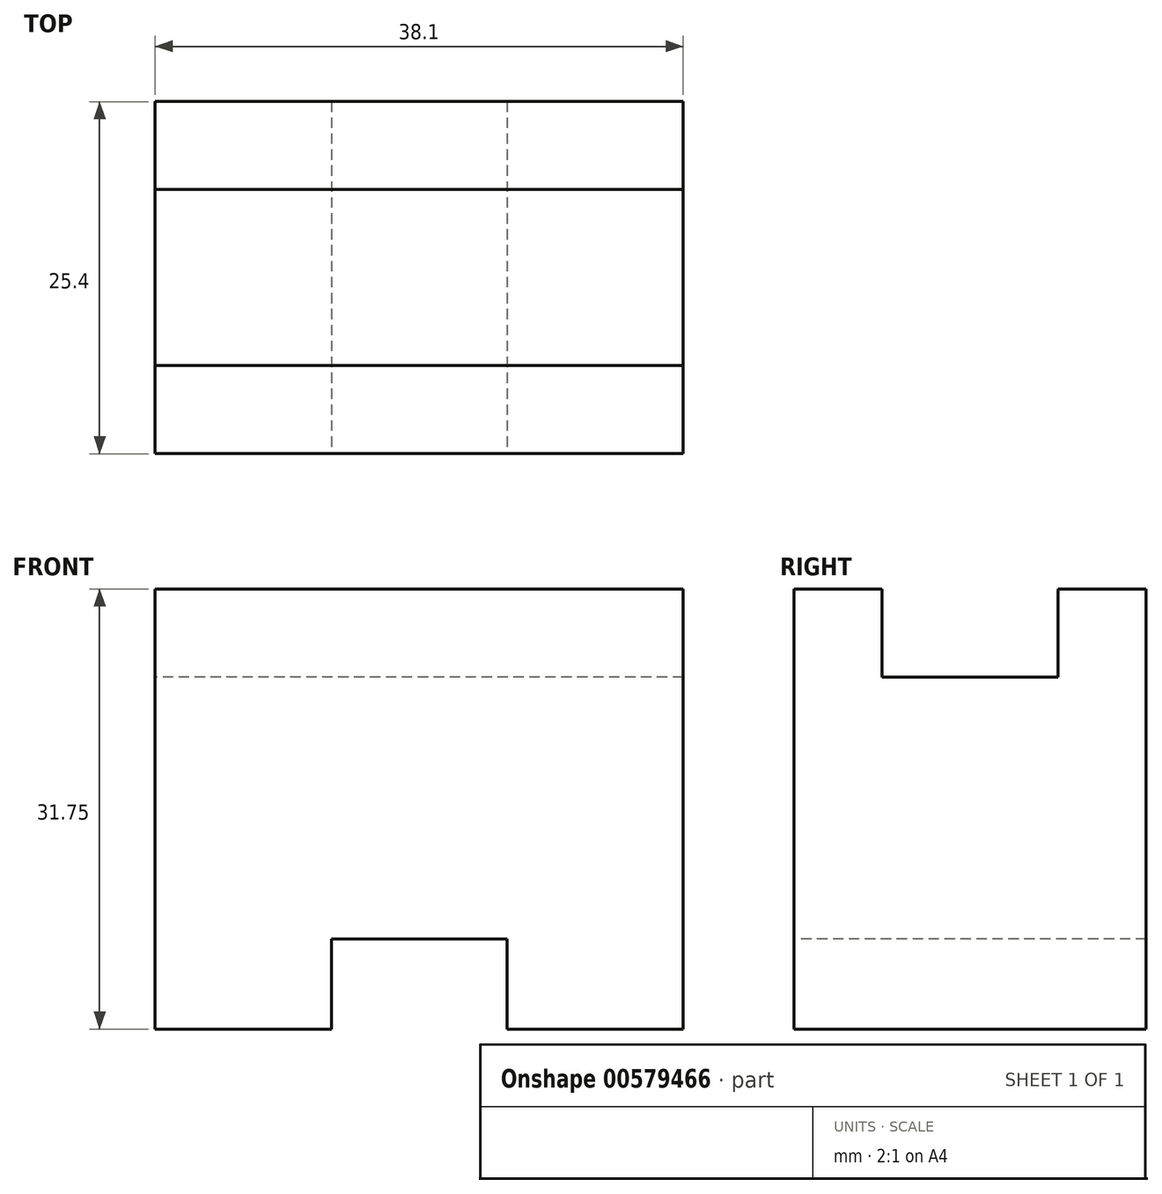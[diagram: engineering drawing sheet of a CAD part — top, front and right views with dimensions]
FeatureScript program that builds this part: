
annotation { "Feature Type Name" : "Feature", "Feature Type Description" : "" }
export const myFeature = defineFeature(function(context is Context, id is Id, definition is map)
    precondition{}
    {
        {
            var Q0;
            Q0=qCreatedBy(makeId("Right.planeOp"),FACE);
            var sketch = newSketch(context, id + "F0", { "sketchPlane" : qUnion([Q0])});
            skLineSegment(sketch, "E0", {"start": v(-37.44, 0) * mm, "end": v(-37.44, 31.75) * mm});
            skLineSegment(sketch, "E1", {"start": v(-37.44, 31.75) * mm, "end": v(-31.09, 31.75) * mm});
            skLineSegment(sketch, "E2", {"start": v(-31.09, 31.75) * mm, "end": v(-31.09, 25.4) * mm});
            skLineSegment(sketch, "E3", {"start": v(-31.09, 25.4) * mm, "end": v(-18.39, 25.4) * mm});
            skLineSegment(sketch, "E4", {"start": v(-18.39, 25.4) * mm, "end": v(-18.39, 31.75) * mm});
            skLineSegment(sketch, "E5", {"start": v(-18.39, 31.75) * mm, "end": v(-12.04, 31.75) * mm});
            skLineSegment(sketch, "E6", {"start": v(-12.04, 31.75) * mm, "end": v(-12.04, 0) * mm});
            skLineSegment(sketch, "E7", {"start": v(-12.04, 0) * mm, "end": v(-37.44, 0) * mm});
            skSolve(sketch);
        }
        {
            var Q0;
            Q0=makeQuery(id+"F0.imprint","IMPRINT",FACE,{"disambiguationData":[TD([[makeQuery(id+"F0.imprint","IMPRINT",EDGE,{"derivedFrom":sQuery(id+"F0.wireOp",EDGE,"E0")}),-1.0]])]});
            extrude(context, id + "F1", {"entities" : qUnion([Q0]), "depth" : 38.1 * mm, "offsetDistance" : 25.4 * mm});
        }
        {
            var Q0;
            Q0=makeQuery(id+"F1.opExtrude","SWEPT_FACE",FACE,{"disambiguationData":[OSD([sQuery(id+"F0.wireOp",EDGE,"E0")])]});
            var sketch = newSketch(context, id + "F2", { "sketchPlane" : qUnion([Q0])});
            skLineSegment(sketch, "E8", {"start": v(12.74, 0) * mm, "end": v(12.74, 6.49) * mm});
            skLineSegment(sketch, "E9", {"start": v(12.74, 6.49) * mm, "end": v(25.39, 6.49) * mm});
            skLineSegment(sketch, "E10", {"start": v(25.39, 6.49) * mm, "end": v(25.39, 0) * mm});
            skSolve(sketch);
        }
        {
            var Q0;
            Q0 = qSketchRegion(id + "F2", true);
            var Q1;
            {var subQ0=sQuery(id+"F2.wireOp",EDGE,"E8");Q1=makeQuery(id+"F2.imprint","IMPRINT",FACE,{"disambiguationData":[TD([[makeQuery(id+"F2.imprint","IMPRINT",EDGE,{"derivedFrom":subQ0}),-1.0]])]});}
            extrude(context, id + "F3", {"entities" : qUnion([Q0, Q1]), "operationType" : NewBodyOperationType.REMOVE, "endBound" : BoundingType.THROUGH_ALL, "oppositeDirection" : true, "depth" : 25.4 * mm, "offsetDistance" : 25.4 * mm});
        }
    });
